# Revit family: LSER22
name_source: partatom
category: Lighting Fixtures
revit_build: Autodesk Revit MEP 2012 (Build: 20110309_2315(x64)
units: mm (PartAtom-declared; Revit-internal decimal feet)

## types (24) — shared parameters
Apparent Load = 0 VA
Color Filter = 16777215
Default Elevation = 4' - 0"
Dimming Lamp Color Temperature Shift = <None>
IES FILE LINK = http://www.columbialighting.com
LEGNTH = 4' - 6"
Manufacturer = COLUMBIA
Model = LSER22
Number of Poles = 1
Power Factor = 1
Product Documentation Link = http://www.columbialighting.com
Product Page URL = http://www.columbialighting.com
Tilt Angle = 90.00°
Voltage = 0 V
WIDTH = 2' - 0"

## per-type parameters (varying)
| type | Photometric Web File |
| LSER22-30HLG-C-ESD | itl78367.ies |
| LSER22-30HLG-R-ESD | itl78368.ies |
| LSER22-30LWG-C-ESD | itl78371.ies |
| LSER22-30LWG-R-ESD | itl78372.ies |
| LSER22-30MLG-C-ESD | itl78353.ies |
| LSER22-30MLG-R-ESD | itl78356.ies |
| LSER22-30VLG-C-ESD | itl78369.ies |
| LSER22-30VLG-R-ESD | itl78370.ies |
| LSER22-35HLG-C-ESD | itl78359.ies |
| LSER22-35HLG-R-ESD | itl78361.ies |
| LSER22-35LWG-C-ESD | itl78349.ies |
| LSER22-35LWG-R-ESD | itl78351.ies |
| LSER22-35MLG-C-ESD | itl78354.ies |
| LSER22-35MLG-R-ESD | itl78357.ies |
| LSER22-35VLG-C-ESD | itl78363.ies |
| LSER22-35VLG-R-ESD | itl78365.ies |
| LSER22-40HLG-C-ESD | itl78360.ies |
| LSER22-40HLG-R-ESD | itl78362.ies |
| LSER22-40LWG-C-ESD | itl78350.ies |
| LSER22-40LWG-R-ESD | itl78352.ies |
| LSER22-40MLG-C-ESD | itl78355.ies |
| LSER22-40MLG-R-ESD | itl78358.ies |
| LSER22-40VLG-C-ESD | itl78364.ies |
| LSER22-40VLG-R-ESD | itl78366.ies |

## geometry (parser evidence)
native form markers: Sweep x2
no freeform markers — native parametric forms only
